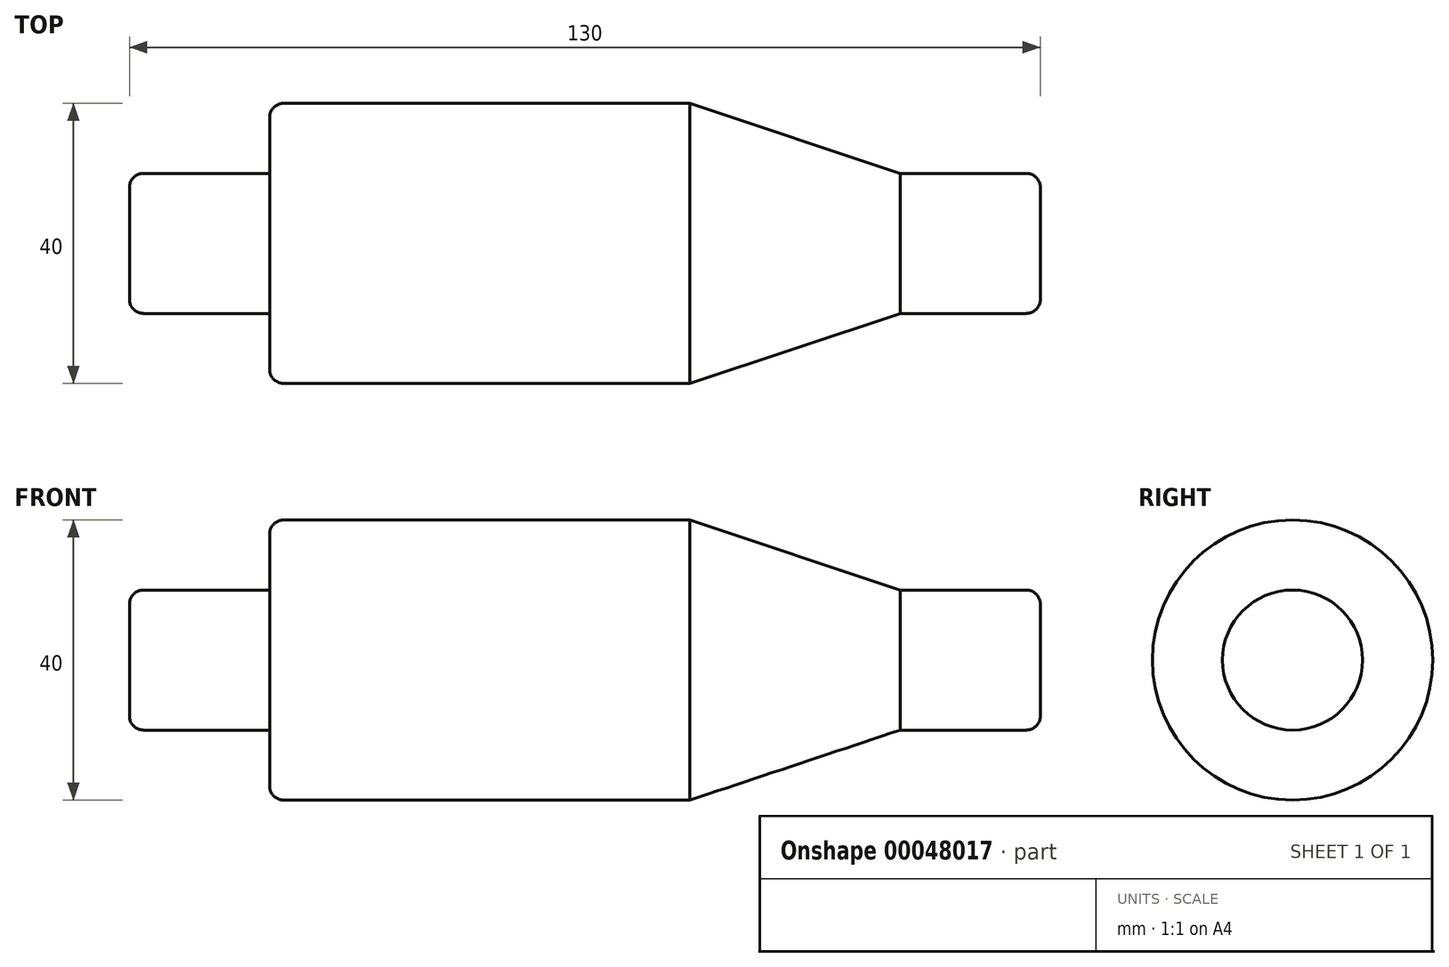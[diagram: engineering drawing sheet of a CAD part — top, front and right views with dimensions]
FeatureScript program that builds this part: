
annotation { "Feature Type Name" : "Feature", "Feature Type Description" : "" }
export const myFeature = defineFeature(function(context is Context, id is Id, definition is map)
    precondition{}
    {
        {
            var Q0;
            Q0=qCreatedBy(makeId("Front.planeOp"),FACE);
            var sketch = newSketch(context, id + "F0", { "sketchPlane" : qUnion([Q0])});
            skLineSegment(sketch, "E0", {"start": v(0, 0) * mm, "end": v(0, 10) * mm});
            skLineSegment(sketch, "E1", {"start": v(0, 10) * mm, "end": v(20, 10) * mm});
            skLineSegment(sketch, "E2", {"start": v(20, 10) * mm, "end": v(20, 20) * mm});
            skLineSegment(sketch, "E3", {"start": v(20, 20) * mm, "end": v(80, 20) * mm});
            skLineSegment(sketch, "E4", {"start": v(80, 20) * mm, "end": v(110, 10) * mm});
            skLineSegment(sketch, "E5", {"start": v(110, 10) * mm, "end": v(130, 10) * mm});
            skLineSegment(sketch, "E6", {"start": v(130, 10) * mm, "end": v(130, 0) * mm});
            skLineSegment(sketch, "E7", {"start": v(130, 0) * mm, "end": v(0, 0) * mm});
            skLineSegment(sketch, "E8", {"start": v(-31.03, 0) * mm, "end": v(147.19, 0) * mm, "construction": true});
            skSolve(sketch);
        }
        {
            var Q0;
            Q0 = qSketchRegion(id + "F0", true);
            var Q1;
            Q1=sQuery(id+"F0.wireOp",EDGE,"E7");
            revolve(context, id + "F1", {"entities" : qUnion([Q0]), "axis" : qUnion([Q1]), "revolveType" : RevolveType.FULL});
        }
        {
            var Q0;
            Q0=makeQuery(id+"F1.opRevolve","SWEPT_EDGE",EDGE,{"disambiguationData":[OSD([sQuery(id+"F0.wireOp",EDGE,"E5"),sQuery(id+"F0.wireOp",EDGE,"E6")])]});
            var Q1;
            Q1=makeQuery(id+"F1.opRevolve","SWEPT_EDGE",EDGE,{"disambiguationData":[OSD([sQuery(id+"F0.wireOp",EDGE,"E2"),sQuery(id+"F0.wireOp",EDGE,"E3")])]});
            var Q2;
            Q2=makeQuery(id+"F1.opRevolve","SWEPT_EDGE",EDGE,{"disambiguationData":[OSD([sQuery(id+"F0.wireOp",EDGE,"E0"),sQuery(id+"F0.wireOp",EDGE,"E1")])]});
            fillet(context, id + "F2", {"entities" : qUnion([Q0, Q1, Q2]), "radius" : 2 * mm, "tangentPropagation" : true, "allowEdgeOverflow" : false});
        }
    });
